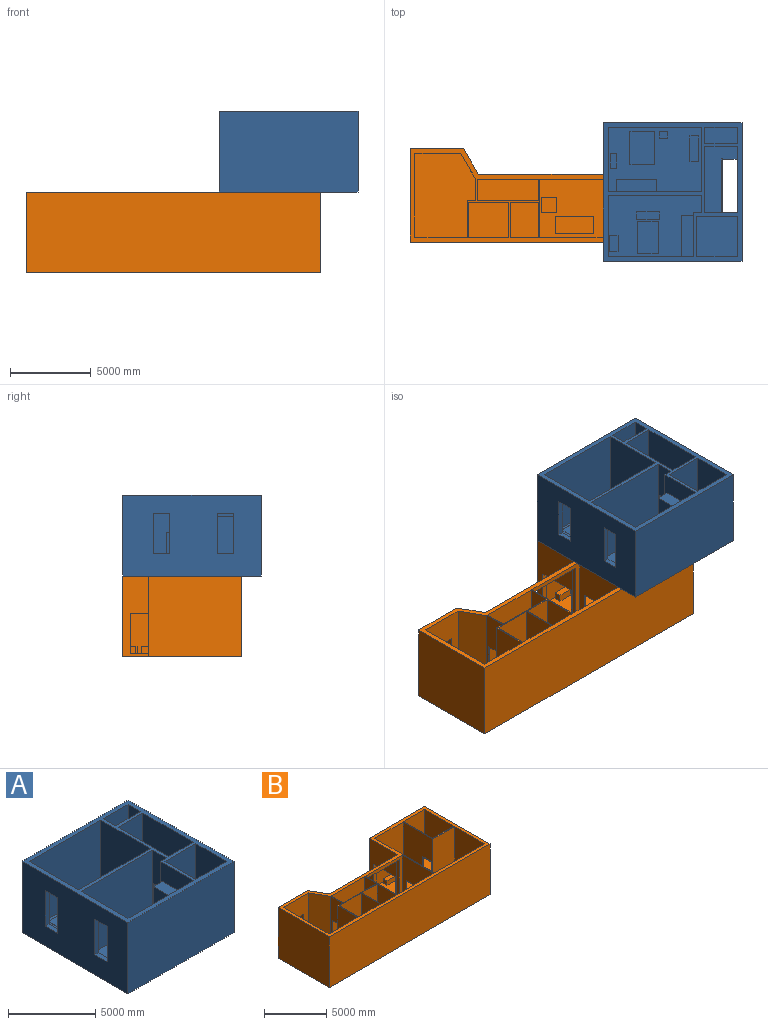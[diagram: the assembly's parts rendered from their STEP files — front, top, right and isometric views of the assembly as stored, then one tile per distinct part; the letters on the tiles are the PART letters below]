
ASSEMBLY  parts=2 mates=1
PART A: 97 faces, bbox 8600x8600x5000 mm
  f0: plane 8000x8000mm, normal (0,0,1), area 45456700mm2, adj f1,f2,f3,f5,f6,f8,f9,f10
  f1: plane 4800x2700mm, normal (-1,0,0), area 4210000mm2, adj f0,f17,f18,f22,f59,f60,f61
  f2: plane 4800x3800mm, normal (1,0,0), area 15740000mm2, adj f0,f17,f18,f20,f50,f51,f52,f53
  f3: plane 4800x4000mm, normal (1,0,0), area 16700000mm2, adj f0,f8,f18,f19,f46,f47,f48,f49
  f4: plane 8600x5000mm, normal (-1,0,0), area 38000000mm2, adj f7,f14,f15,f18,f46,f47,f48,f49
  f5: plane 4800x2500mm, normal (0,-1,0), area 10125000mm2, adj f0,f13,f18,f23,f43,f44,f45
  f6: plane 4800x4100mm, normal (1,0,0), area 15930000mm2, adj f0,f18,f24,f25,f34,f35,f36,f37
  f7: plane 8600x8600mm, normal (0,0,-1), area 70861250mm2, adj f4,f9,f14,f15,f16,f24,f31,f33
  f8: plane 5800x4800mm, normal (0,-1,0), area 27840000mm2, adj f0,f3,f18,f28
  f9: plane 5000x4100mm, normal (-1,0,0), area 20350000mm2, adj f0,f7,f18,f24,f25,f33
  f10: plane 4800x1000mm, normal (-1,0,0), area 4800000mm2, adj f0,f12,f18,f26
  f11: plane 4800x2500mm, normal (0,1,0), area 12000000mm2, adj f0,f13,f18,f23
  f12: plane 4800x2000mm, normal (0,-1,0), area 9600000mm2, adj f0,f10,f18,f27
  f13: plane 4800x2500mm, normal (-1,0,0), area 12000000mm2, adj f0,f5,f11,f18
  f14: plane 8600x5000mm, normal (0,1,0), area 43000000mm2, adj f4,f7,f16,f18
  f15: plane 8600x5000mm, normal (0,-1,0), area 43000000mm2, adj f4,f7,f16,f18
  f16: plane 8600x5000mm, normal (1,0,0), area 43000000mm2, adj f7,f14,f15,f18
  f17: plane 5300x4800mm, normal (0,1,0), area 25440000mm2, adj f0,f1,f2,f18
  f18: plane 8600x8600mm, normal (0,0,1), area 13620000mm2, adj f1,f2,f3,f4,f5,f6,f8,f9
  f19: plane 5800x4800mm, normal (0,1,0), area 19090000mm2, adj f0,f3,f18,f28,f54,f56,f57
  f20: plane 5800x4800mm, normal (0,-1,0), area 27840000mm2, adj f0,f2,f18,f21
  f21: plane 4800x1100mm, normal (-1,0,0), area 3405000mm2, adj f0,f18,f20,f22,f37,f38,f39
  f22: plane 4800x500mm, normal (0,1,0), area 2400000mm2, adj f0,f1,f18,f21
  f23: plane 4800x2500mm, normal (1,0,0), area 12000000mm2, adj f0,f5,f11,f18
  f24: plane 5000x2000mm, normal (0,1,0), area 7835000mm2, adj f0,f6,f7,f9,f18,f30,f31,f32
  f25: plane 4800x2000mm, normal (0,-1,0), area 7725000mm2, adj f0,f6,f9,f18,f40,f41,f42
  f26: plane 4800x2000mm, normal (0,1,0), area 7725000mm2, adj f0,f10,f18,f27,f40,f41,f42
  f27: plane 4800x1000mm, normal (1,0,0), area 4800000mm2, adj f0,f12,f18,f26
  f28: plane 4800x4000mm, normal (-1,0,0), area 17325000mm2, adj f0,f8,f18,f19,f34,f35,f36
  f29: plane 1000x75mm, normal (0,1,0), area 75000mm2, adj f0,f30,f31,f32
  f30: plane 3350x1000mm, normal (-1,0,0), area 3350000mm2, adj f0,f24,f29,f32
  f31: plane 3350x1200mm, normal (1,0,0), area 4020000mm2, adj f7,f24,f29,f32,f33
  f32: plane 3350x75mm, normal (0,0,1), area 251250mm2, adj f24,f29,f30,f31
  f33: plane 925x200mm, normal (0,-1,0), area 185000mm2, adj f0,f7,f9,f31
  f34: plane 2500x200mm, normal (0,1,0), area 500000mm2, adj f0,f6,f28,f36
  f35: plane 2500x200mm, normal (0,-1,0), area 500000mm2, adj f0,f6,f28,f36
  f36: plane 750x200mm, normal (0,0,-1), area 150000mm2, adj f6,f28,f34,f35
  f37: plane 2500x200mm, normal (0,1,0), area 500000mm2, adj f0,f6,f21,f39
  f38: plane 2500x200mm, normal (0,-1,0), area 500000mm2, adj f0,f6,f21,f39
  f39: plane 750x200mm, normal (0,0,-1), area 150000mm2, adj f6,f21,f37,f38
  f40: plane 2500x200mm, normal (-1,0,0), area 500000mm2, adj f0,f25,f26,f42
  f41: plane 2500x200mm, normal (1,0,0), area 500000mm2, adj f0,f25,f26,f42
  f42: plane 750x200mm, normal (0,0,-1), area 150000mm2, adj f25,f26,f40,f41
  f43: plane 2500x200mm, normal (1,0,0), area 500000mm2, adj f0,f5,f24,f44
  f44: plane 750x200mm, normal (0,0,-1), area 150000mm2, adj f5,f24,f43,f45
  f45: plane 2500x200mm, normal (-1,0,0), area 500000mm2, adj f0,f5,f24,f44
  f46: plane 1000x300mm, normal (0,0,-1), area 300000mm2, adj f3,f4,f47,f49
  f47: plane 2500x300mm, normal (0,1,0), area 750000mm2, adj f3,f4,f46,f48
  f48: plane 1000x300mm, normal (0,0,1), area 300000mm2, adj f3,f4,f47,f49
  f49: plane 2500x300mm, normal (0,-1,0), area 750000mm2, adj f3,f4,f46,f48
  f50: plane 1000x300mm, normal (0,0,-1), area 300000mm2, adj f2,f4,f51,f53
  f51: plane 2500x300mm, normal (0,1,0), area 750000mm2, adj f2,f4,f50,f52
  f52: plane 1000x300mm, normal (0,0,1), area 300000mm2, adj f2,f4,f51,f53
  f53: plane 2500x300mm, normal (0,-1,0), area 750000mm2, adj f2,f4,f50,f52
  f54: plane 3500x750mm, normal (1,0,0), area 2625000mm2, adj f0,f19,f55,f57
  f55: plane 3500x2500mm, normal (0,1,0), area 8750000mm2, adj f0,f54,f56,f57
  f56: plane 3500x750mm, normal (-1,0,0), area 2625000mm2, adj f0,f19,f55,f57
  f57: plane 2500x750mm, normal (0,0,1), area 1875000mm2, adj f19,f54,f55,f56
  f58: plane 3500x2500mm, normal (-1,0,0), area 8750000mm2, adj f0,f59,f60,f61
  f59: plane 3500x750mm, normal (0,-1,0), area 2625000mm2, adj f0,f1,f58,f61
  f60: plane 3500x750mm, normal (0,1,0), area 2625000mm2, adj f0,f1,f58,f61
  f61: plane 2500x750mm, normal (0,0,1), area 1875000mm2, adj f1,f58,f59,f60
  f62: plane 2100x25mm, normal (-1,0,0), area 52500mm2, adj f0,f63,f65,f66
  f63: plane 1500x25mm, normal (0,-1,0), area 37500mm2, adj f0,f62,f64,f66
  f64: plane 2100x25mm, normal (1,0,0), area 52500mm2, adj f0,f63,f65,f66
  f65: plane 1500x25mm, normal (0,1,0), area 37500mm2, adj f0,f62,f64,f66
  f66: plane 2100x1500mm, normal (0,0,1), area 3150000mm2, adj f62,f63,f64,f65
  f67: plane 530x25mm, normal (0,-1,0), area 13250mm2, adj f0,f68,f70,f71
  f68: plane 430x25mm, normal (1,0,0), area 10750mm2, adj f0,f67,f69,f71
  f69: plane 530x25mm, normal (0,1,0), area 13250mm2, adj f0,f68,f70,f71
  f70: plane 430x25mm, normal (-1,0,0), area 10750mm2, adj f0,f67,f69,f71
  f71: plane 530x430mm, normal (0,0,1), area 227900mm2, adj f67,f68,f69,f70
  f72: plane 550x25mm, normal (0,1,0), area 13750mm2, adj f0,f73,f75,f76
  f73: plane 1600x25mm, normal (-1,0,0), area 40000mm2, adj f0,f72,f74,f76
  f74: plane 550x25mm, normal (0,-1,0), area 13750mm2, adj f0,f73,f75,f76
  f75: plane 1600x25mm, normal (1,0,0), area 40000mm2, adj f0,f72,f74,f76
  f76: plane 1600x550mm, normal (0,0,1), area 880000mm2, adj f72,f73,f74,f75
  f77: plane 380x25mm, normal (0,1,0), area 9500mm2, adj f0,f78,f80,f81
  f78: plane 930x25mm, normal (-1,0,0), area 23250mm2, adj f0,f77,f79,f81
  f79: plane 380x25mm, normal (0,-1,0), area 9500mm2, adj f0,f78,f80,f81
  f80: plane 930x25mm, normal (1,0,0), area 23250mm2, adj f0,f77,f79,f81
  f81: plane 930x380mm, normal (0,0,1), area 353400mm2, adj f77,f78,f79,f80
  f82: plane 1300x25mm, normal (0,1,0), area 32500mm2, adj f0,f83,f85,f86
  f83: plane 2000x25mm, normal (-1,0,0), area 50000mm2, adj f0,f82,f84,f86
  f84: plane 1300x25mm, normal (0,-1,0), area 32500mm2, adj f0,f83,f85,f86
  f85: plane 2000x25mm, normal (1,0,0), area 50000mm2, adj f0,f82,f84,f86
  f86: plane 2000x1300mm, normal (0,0,1), area 2600000mm2, adj f82,f83,f84,f85
  f87: plane 1000x25mm, normal (1,0,0), area 25000mm2, adj f0,f88,f90,f91
  f88: plane 500x25mm, normal (0,1,0), area 12500mm2, adj f0,f87,f89,f91
  f89: plane 1000x25mm, normal (-1,0,0), area 25000mm2, adj f0,f88,f90,f91
  f90: plane 500x25mm, normal (0,-1,0), area 12500mm2, adj f0,f87,f89,f91
  f91: plane 1000x500mm, normal (0,0,1), area 500000mm2, adj f87,f88,f89,f90
  f92: plane 1400x25mm, normal (0,1,0), area 35000mm2, adj f0,f93,f95,f96
  f93: plane 480x25mm, normal (-1,0,0), area 12000mm2, adj f0,f92,f94,f96
  f94: plane 1400x25mm, normal (0,-1,0), area 35000mm2, adj f0,f93,f95,f96
  f95: plane 480x25mm, normal (1,0,0), area 12000mm2, adj f0,f92,f94,f96
  f96: plane 1400x480mm, normal (0,0,1), area 672000mm2, adj f92,f93,f94,f95
PART B: 112 faces, bbox 18300x7400x5000 mm
  f0: plane 4800x4200mm, normal (0,-1,0), area 3060000mm2, adj f5,f7,f30,f31,f65,f66,f67
  f1: plane 6800x4800mm, normal (1,0,0), area 21390000mm2, adj f15,f16,f30,f31,f50,f51,f52,f62
  f2: plane 4800x2850mm, normal (0,-1,0), area 9180000mm2, adj f21,f29,f30,f31,f59,f60,f61
  f3: plane 5000x3323.21mm, normal (0,1,0), area 12116025.4mm2, adj f23,f24,f30,f31,f32,f59,f60,f61
  f4: plane 4800x1350mm, normal (1,0,0), area 4605000mm2, adj f9,f30,f31,f37,f56,f57,f58
  f5: plane 4800x3600mm, normal (1,0,0), area 15405000mm2, adj f0,f12,f30,f31,f53,f54,f55
  f6: plane 4800x1350mm, normal (-1,0,0), area 4605000mm2, adj f9,f30,f31,f37,f53,f54,f55
  f7: plane 4800x3600mm, normal (-1,0,0), area 12280000mm2, adj f0,f12,f30,f31,f50,f51,f52
  f8: plane 4800x16.24mm, normal (0,-1,0), area 77949.9mm2, adj f29,f30,f31,f38
  f9: plane 4800x3800mm, normal (0,-1,0), area 18240000mm2, adj f4,f6,f30,f31
  f10: plane 4800x2500mm, normal (0,1,0), area 12000000mm2, adj f14,f30,f41,f43
  f11: plane 4800x1750mm, normal (0,1,0), area 8400000mm2, adj f13,f30,f44,f46
  f12: plane 4800x4200mm, normal (0,1,0), area 20160000mm2, adj f5,f7,f30,f31
  f13: plane 2180x1750mm, normal (0,0,1), area 3815000mm2, adj f11,f44,f45,f46
  f14: plane 2500x2180mm, normal (0,0,1), area 5450000mm2, adj f10,f41,f42,f43
  f15: plane 5700x4800mm, normal (0,1,0), area 27360000mm2, adj f1,f19,f30,f31
  f16: plane 4800x3230mm, normal (0,-1,0), area 15504000mm2, adj f1,f30,f31,f33
  f17: plane 4800x3300mm, normal (-1,0,0), area 15840000mm2, adj f18,f30,f31,f35
  f18: plane 4800x2400mm, normal (0,-1,0), area 11520000mm2, adj f17,f30,f31,f36
  f19: plane 4800x3430mm, normal (-1,0,0), area 16464000mm2, adj f15,f30,f31,f34
  f20: plane 4800x3270mm, normal (0,1,0), area 15696000mm2, adj f21,f30,f31,f40
  f21: plane 5200x4800mm, normal (1,0,0), area 24960000mm2, adj f2,f20,f30,f31
  f22: plane 7753.03x5000mm, normal (0,1,0), area 21665172.4mm2, adj f23,f28,f30,f31,f32,f65,f66,f67
  f23: plane 5000x1600mm, normal (0.87,0.5,0), area 9237604.3mm2, adj f3,f22,f30,f32
  f24: plane 5800x5000mm, normal (-1,0,0), area 29000000mm2, adj f3,f25,f30,f32
  f25: plane 18300x5000mm, normal (0,-1,0), area 91500000mm2, adj f24,f26,f30,f32
  f26: plane 7400x5000mm, normal (1,0,0), area 37000000mm2, adj f25,f27,f30,f32
  f27: plane 6300x5000mm, normal (0,1,0), area 31500000mm2, adj f26,f28,f30,f32
  f28: plane 5000x3200mm, normal (-1,0,0), area 9750000mm2, adj f22,f27,f30,f31,f32,f62,f63,f64
  f29: plane 4800x1600mm, normal (-0.87,-0.5,0), area 8868100.1mm2, adj f2,f8,f30,f31
  f30: plane 18300x7400mm, normal (0,0,1), area 17432028.1mm2, adj f0,f1,f2,f3,f4,f5,f6,f7
  f31: plane 17700x6800mm, normal (0,0,1), area 71969640mm2, adj f0,f1,f2,f3,f4,f5,f6,f7
  f32: plane 18300x7400mm, normal (0,0,-1), area 103076136.5mm2, adj f3,f22,f23,f24,f25,f26,f27,f28
  f33: plane 4800x3370mm, normal (-1,0,0), area 13801000mm2, adj f16,f30,f31,f34,f47,f48,f49
  f34: plane 4800x2470mm, normal (0,-1,0), area 11856000mm2, adj f19,f30,f31,f33
  f35: plane 4800x2400mm, normal (0,1,0), area 11520000mm2, adj f17,f30,f31,f36
  f36: plane 4800x3300mm, normal (1,0,0), area 13465000mm2, adj f18,f30,f31,f35,f47,f48,f49
  f37: plane 4800x3800mm, normal (0,1,0), area 18240000mm2, adj f4,f6,f30,f31
  f38: plane 4800x1350mm, normal (-1,0,0), area 4605000mm2, adj f8,f30,f31,f39,f56,f57,f58
  f39: plane 4800x520mm, normal (0,1,0), area 2496000mm2, adj f30,f31,f38,f40
  f40: plane 4800x2250mm, normal (-1,0,0), area 10800000mm2, adj f20,f30,f31,f39
  f41: plane 4800x2180mm, normal (1,0,0), area 10464000mm2, adj f10,f14,f30,f42
  f42: plane 4800x2500mm, normal (0,-1,0), area 12000000mm2, adj f14,f30,f41,f43
  f43: plane 4800x2180mm, normal (-1,0,0), area 10464000mm2, adj f10,f14,f30,f42
  f44: plane 4800x2180mm, normal (1,0,0), area 10464000mm2, adj f11,f13,f30,f45
  f45: plane 4800x1750mm, normal (0,-1,0), area 8400000mm2, adj f13,f30,f44,f46
  f46: plane 4800x2180mm, normal (-1,0,0), area 10464000mm2, adj f11,f13,f30,f45
  f47: plane 2500x70mm, normal (0,1,0), area 175000mm2, adj f31,f33,f36,f49
  f48: plane 2500x70mm, normal (0,-1,0), area 175000mm2, adj f31,f33,f36,f49
  f49: plane 950x70mm, normal (0,0,-1), area 66500mm2, adj f33,f36,f47,f48
  f50: plane 2500x70mm, normal (0,-1,0), area 175000mm2, adj f1,f7,f31,f51
  f51: plane 2000x70mm, normal (0,0,-1), area 140000mm2, adj f1,f7,f50,f52
  f52: plane 2500x70mm, normal (0,1,0), area 175000mm2, adj f1,f7,f31,f51
  f53: plane 750x70mm, normal (0,0,-1), area 52500mm2, adj f5,f6,f54,f55
  f54: plane 2500x70mm, normal (0,-1,0), area 175000mm2, adj f5,f6,f31,f53
  f55: plane 2500x70mm, normal (0,1,0), area 175000mm2, adj f5,f6,f31,f53
  f56: plane 2500x70mm, normal (0,1,0), area 175000mm2, adj f4,f31,f38,f58
  f57: plane 2500x70mm, normal (0,-1,0), area 175000mm2, adj f4,f31,f38,f58
  f58: plane 750x70mm, normal (0,0,-1), area 52500mm2, adj f4,f38,f56,f57
  f59: plane 3000x300mm, normal (1,0,0), area 900000mm2, adj f2,f3,f31,f61
  f60: plane 3000x300mm, normal (-1,0,0), area 900000mm2, adj f2,f3,f31,f61
  f61: plane 1500x300mm, normal (0,0,-1), area 450000mm2, adj f2,f3,f59,f60
  f62: plane 2500x300mm, normal (0,-1,0), area 750000mm2, adj f1,f28,f31,f63
  f63: plane 2500x300mm, normal (0,0,-1), area 750000mm2, adj f1,f28,f62,f64
  f64: plane 2500x300mm, normal (0,1,0), area 750000mm2, adj f1,f28,f31,f63
  f65: plane 4500x300mm, normal (-1,0,0), area 1350000mm2, adj f0,f22,f31,f66
  f66: plane 3800x300mm, normal (0,0,-1), area 1140000mm2, adj f0,f22,f65,f67
  f67: plane 4500x300mm, normal (1,0,0), area 1350000mm2, adj f0,f22,f31,f66
  f68: plane 700x440mm, normal (0,1,0), area 308000mm2, adj f31,f69,f71,f72
  f69: plane 1500x440mm, normal (-1,0,0), area 660000mm2, adj f31,f68,f70,f72
  f70: plane 700x440mm, normal (0,-1,0), area 308000mm2, adj f31,f69,f71,f72
  f71: plane 1500x440mm, normal (1,0,0), area 660000mm2, adj f31,f68,f70,f72
  f72: plane 1500x700mm, normal (0,0,1), area 1050000mm2, adj f68,f69,f70,f71
  f73: plane 630x440mm, normal (0,1,0), area 277200mm2, adj f31,f74,f76,f77
  f74: plane 440x430mm, normal (-1,0,0), area 189200mm2, adj f31,f73,f75,f77
  f75: plane 630x440mm, normal (0,-1,0), area 277200mm2, adj f31,f74,f76,f77
  f76: plane 440x430mm, normal (1,0,0), area 189200mm2, adj f31,f73,f75,f77
  f77: plane 630x430mm, normal (0,0,1), area 270900mm2, adj f73,f74,f75,f76
  f78: plane 1100x440mm, normal (1,0,0), area 484000mm2, adj f31,f79,f81,f82
  f79: plane 2370x440mm, normal (0,1,0), area 1042800mm2, adj f31,f78,f80,f82
  f80: plane 1100x440mm, normal (-1,0,0), area 484000mm2, adj f31,f79,f81,f82
  f81: plane 2370x440mm, normal (0,-1,0), area 1042800mm2, adj f31,f78,f80,f82
  f82: plane 2370x1100mm, normal (0,0,1), area 2607000mm2, adj f78,f79,f80,f81
  f83: plane 975x440mm, normal (0,1,0), area 429000mm2, adj f31,f84,f86,f87
  f84: plane 975x440mm, normal (-1,0,0), area 429000mm2, adj f31,f83,f85,f87
  f85: plane 975x440mm, normal (0,-1,0), area 429000mm2, adj f31,f84,f86,f87
  f86: plane 975x440mm, normal (1,0,0), area 429000mm2, adj f31,f83,f85,f87
  f87: plane 975x975mm, normal (0,0,1), area 950625mm2, adj f83,f84,f85,f86
  f88: plane 950x440mm, normal (0,1,0), area 418000mm2, adj f31,f89,f91,f92
  f89: plane 440x420mm, normal (-1,0,0), area 184800mm2, adj f31,f88,f90,f92
  f90: plane 950x440mm, normal (0,-1,0), area 418000mm2, adj f31,f89,f91,f92
  f91: plane 440x420mm, normal (1,0,0), area 184800mm2, adj f31,f88,f90,f92
  f92: plane 950x420mm, normal (0,0,1), area 399000mm2, adj f88,f89,f90,f91
  f93: plane 440x257.52mm, normal (0.78,-0.63,0), area 145803.2mm2, adj f31,f94,f100,f101
  f94: plane 440x329.56mm, normal (0.99,0.1,0), area 145803.2mm2, adj f31,f93,f95,f101
  f95: plane 440x257.52mm, normal (0.63,0.78,0), area 145803.2mm2, adj f31,f94,f96,f101
  f96: plane 440x329.56mm, normal (-0.1,0.99,0), area 145803.2mm2, adj f31,f95,f97,f101
  f97: plane 440x257.52mm, normal (-0.78,0.63,0), area 145803.2mm2, adj f31,f96,f98,f101
  f98: plane 440x329.56mm, normal (-0.99,-0.1,0), area 145803.2mm2, adj f31,f97,f99,f101
  f99: plane 440x257.52mm, normal (-0.63,-0.78,0), area 145803.2mm2, adj f31,f98,f100,f101
  f100: plane 440x329.56mm, normal (0.1,-0.99,0), area 145803.2mm2, adj f31,f93,f99,f101
  f101: plane 830.25x830.25mm, normal (0,0,1), area 530193.4mm2, adj f93,f94,f95,f96,f97,f98,f99,f100
  f102: plane 1530x440mm, normal (0,-1,0), area 673200mm2, adj f31,f103,f105,f106
  f103: plane 525x440mm, normal (1,0,0), area 231000mm2, adj f31,f102,f104,f106
  f104: plane 1530x440mm, normal (0,1,0), area 673200mm2, adj f31,f103,f105,f106
  f105: plane 525x440mm, normal (-1,0,0), area 231000mm2, adj f31,f102,f104,f106
  f106: plane 1530x525mm, normal (0,0,1), area 803250mm2, adj f102,f103,f104,f105
  f107: plane 450x440mm, normal (-1,0,0), area 198000mm2, adj f31,f108,f110,f111
  f108: plane 1000x440mm, normal (0,-1,0), area 440000mm2, adj f31,f107,f109,f111
  f109: plane 450x440mm, normal (1,0,0), area 198000mm2, adj f31,f108,f110,f111
  f110: plane 1000x440mm, normal (0,1,0), area 440000mm2, adj f31,f107,f109,f111
  f111: plane 1000x450mm, normal (0,0,1), area 450000mm2, adj f107,f108,f109,f110
PLACE A t=(1693.63,214.49,5844.12)mm
PLACE B t=(1693.63,1014.49,844.12)mm fixed
MATE fastened A.f7 <-> B.f30  axis (0,0,-1) through (1393.63,4514.49,5644.12)mm
